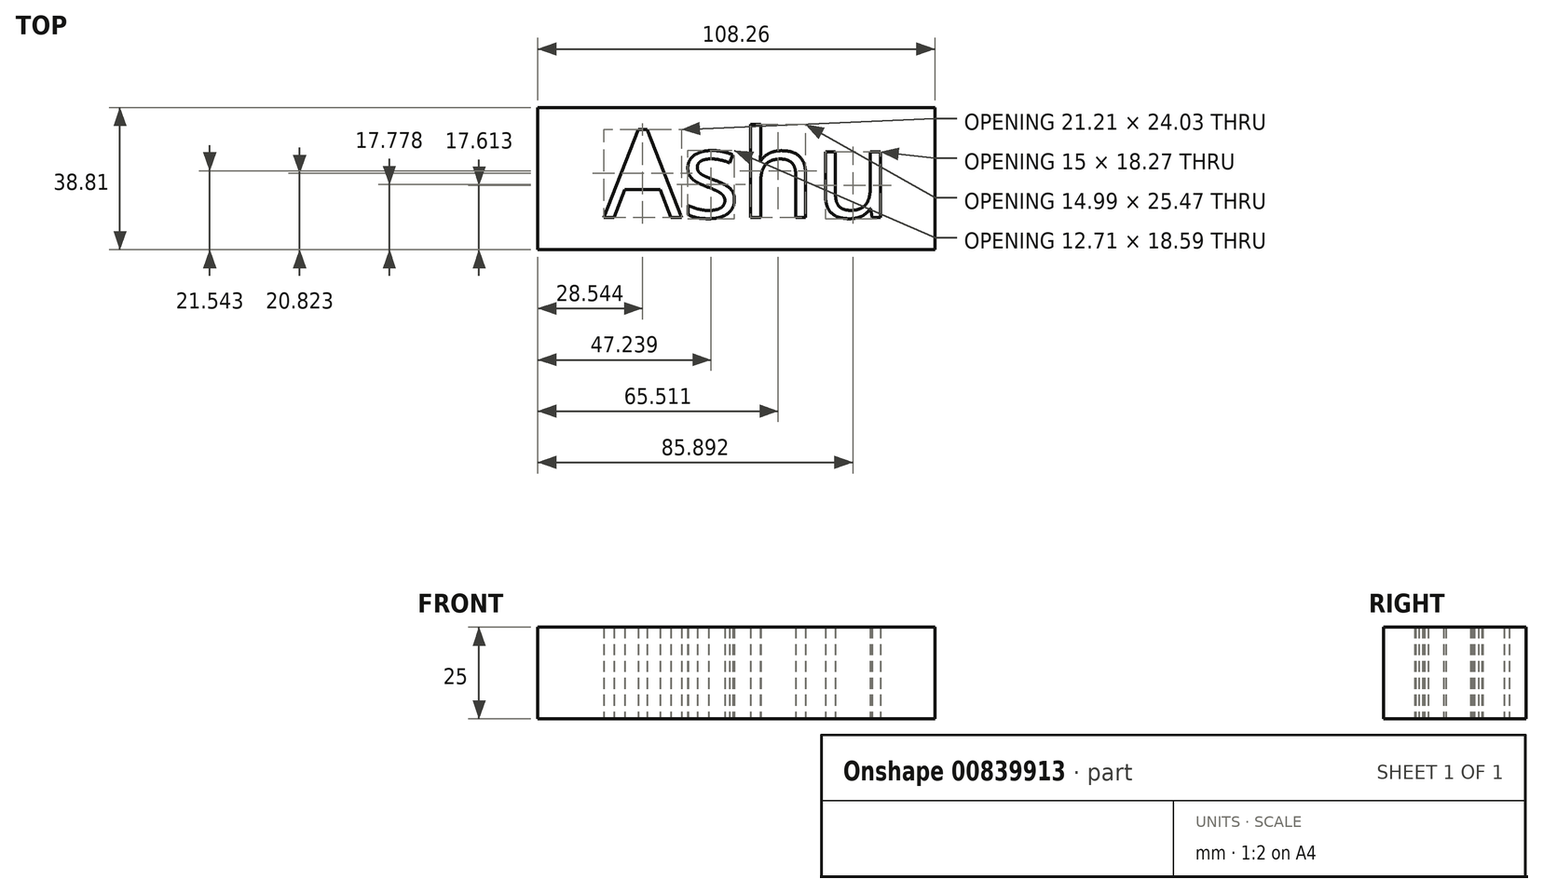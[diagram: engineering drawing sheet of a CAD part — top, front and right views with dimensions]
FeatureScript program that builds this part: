
annotation { "Feature Type Name" : "Feature", "Feature Type Description" : "" }
export const myFeature = defineFeature(function(context is Context, id is Id, definition is map)
    precondition{}
    {
        {
            var Q0;
            Q0=qCreatedBy(makeId("Top.planeOp"),FACE);
            var sketch = newSketch(context, id + "F0", { "sketchPlane" : qUnion([Q0])});
            skLineSegment(sketch, "E0.bottom", {"start": v(-53.97, 11.74) * mm, "end": v(54.3, 11.74) * mm});
            skLineSegment(sketch, "E0.top", {"start": v(-53.97, -27.07) * mm, "end": v(54.3, -27.07) * mm});
            skLineSegment(sketch, "E0.left", {"start": v(-53.97, 11.74) * mm, "end": v(-53.97, -27.07) * mm});
            skLineSegment(sketch, "E0.right", {"start": v(54.3, 11.74) * mm, "end": v(54.3, -27.07) * mm});
            skText(sketch, "E1", { "text": "Ashu", "fontName": "OpenSans-Regular.ttf"});
            const initialGuessF0  = {"E1": [-0.03603, -0.01826, 1, 0, 0.02413]};
            skSetInitialGuess(sketch, initialGuessF0);
            skSolve(sketch);
        }
        {
            var Q0;
            Q0 = qSketchRegion(id + "F0", true);
            extrude(context, id + "F1", {"entities" : qUnion([Q0]), "depth" : 25 * mm, "offsetDistance" : 25 * mm});
        }
    });
